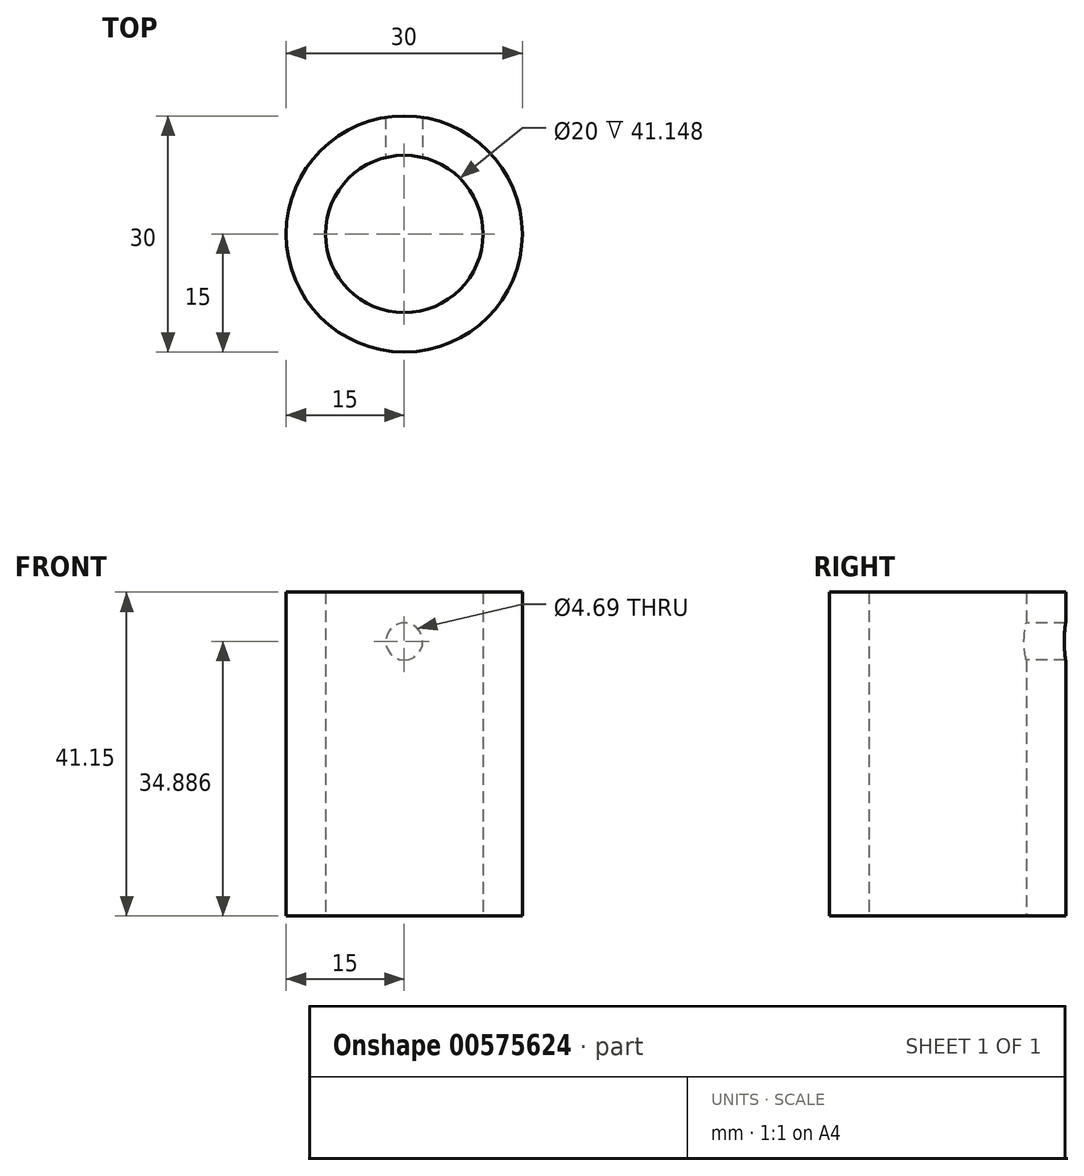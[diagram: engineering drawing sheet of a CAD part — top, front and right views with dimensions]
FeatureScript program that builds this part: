
annotation { "Feature Type Name" : "Feature", "Feature Type Description" : "" }
export const myFeature = defineFeature(function(context is Context, id is Id, definition is map)
    precondition{}
    {
        {
            var Q0;
            Q0=qCreatedBy(makeId("Top.planeOp"),FACE);
            var sketch = newSketch(context, id + "F0", { "sketchPlane" : qUnion([Q0])});
            skCircle(sketch, "E0", {"center": v(0, 0) * mm, "radius": 15 * mm});
            skCircle(sketch, "E1", {"center": v(0, 0) * mm, "radius": 10 * mm});
            skSolve(sketch);
        }
        {
            var Q0;
            Q0 = qSketchRegion(id + "F0", true);
            extrude(context, id + "F1", {"entities" : qUnion([Q0]), "depth" : 41.15 * mm, "offsetDistance" : 25.4 * mm});
        }
        {
            var Q0;
            Q0=qCreatedBy(makeId("Front.planeOp"),FACE);
            var sketch = newSketch(context, id + "F2", { "sketchPlane" : qUnion([Q0])});
            skCircle(sketch, "E2", {"center": v(0, 34.89) * mm, "radius": 2.35 * mm});
            skSolve(sketch);
        }
        {
            var Q0;
            Q0 = qSketchRegion(id + "F2", true);
            extrude(context, id + "F3", {"entities" : qUnion([Q0]), "operationType" : NewBodyOperationType.REMOVE, "oppositeDirection" : true, "depth" : 25.4 * mm, "offsetDistance" : 25.4 * mm});
        }
    });
